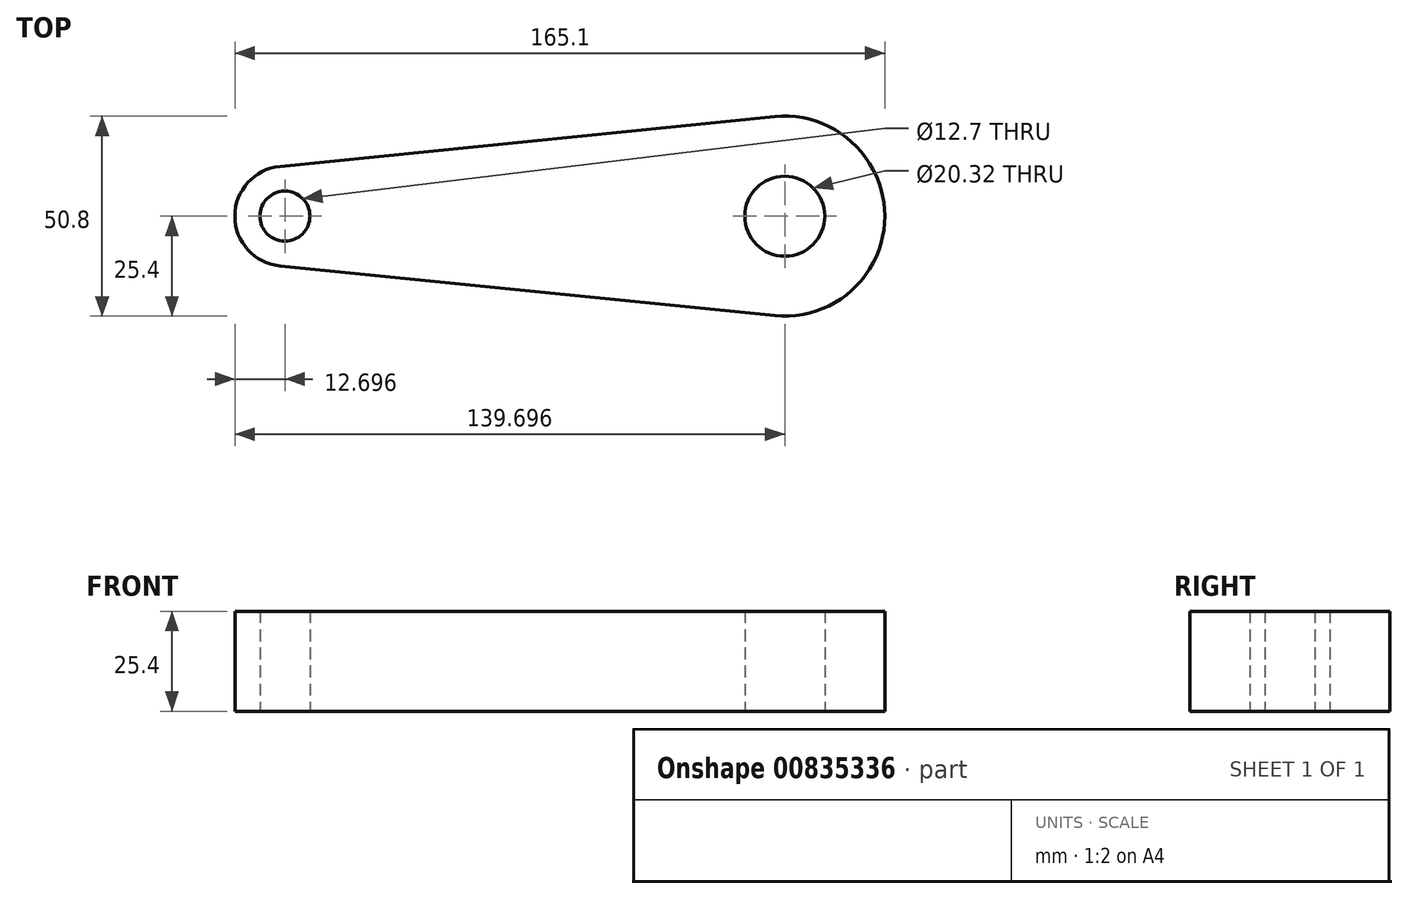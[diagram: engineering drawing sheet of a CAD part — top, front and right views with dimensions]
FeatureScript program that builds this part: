
annotation { "Feature Type Name" : "Feature", "Feature Type Description" : "" }
export const myFeature = defineFeature(function(context is Context, id is Id, definition is map)
    precondition{}
    {
        {
            var Q0;
            Q0=qCreatedBy(makeId("Top.planeOp"),FACE);
            var sketch = newSketch(context, id + "F0", { "sketchPlane" : qUnion([Q0])});
            skCircle(sketch, "E0", {"center": v(-61.43, 0) * mm, "radius": 6.35 * mm});
            skCircle(sketch, "E1", {"center": v(65.57, 0) * mm, "radius": 10.16 * mm});
            skArc(sketch, "E2", {"start": v(-62.7, 12.64) * mm, "mid": v(-74.13, 0) * mm, "end": v(-62.7, -12.64) * mm});
            skArc(sketch, "E3", {"start": v(63.03, -25.27) * mm, "mid": v(90.97, 0) * mm, "end": v(63.03, 25.27) * mm});
            skLineSegment(sketch, "E4", {"start": v(-62.7, -12.64) * mm, "end": v(63.03, -25.27) * mm});
            skLineSegment(sketch, "E5", {"start": v(-62.7, 12.64) * mm, "end": v(63.03, 25.27) * mm});
            skSolve(sketch);
        }
        {
            var Q0;
            Q0=makeQuery(id+"F0.imprint","IMPRINT",FACE,{"disambiguationData":[TD([[makeQuery(id+"F0.imprint","IMPRINT",EDGE,{"derivedFrom":sQuery(id+"F0.wireOp",EDGE,"E0")}),-1.0]])]});
            extrude(context, id + "F1", {"entities" : qUnion([Q0]), "depth" : 25.4 * mm, "offsetDistance" : 25.4 * mm});
        }
    });
